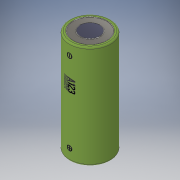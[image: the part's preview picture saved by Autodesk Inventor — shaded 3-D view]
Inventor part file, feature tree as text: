
AUTODESK INVENTOR PART (.ipt)
format: ipt  version: 2019.2 (Build 232265000, 265)  size: 1,053,696 bytes
history: native  units: mm
features: sketch x5, fillet x3, extrude x2, emboss x2, revolve x1, plane x1
ambient origin geometry x8: Origin, YZ Plane, XZ Plane, XY Plane, X Axis, Y Axis, Z Axis, Center Point
bodies: Solid1 (feature_tree)
feature tree (14):
  revolve  "Revolution1"  [1 undecoded]
  fillet  "Fillet1"  [1 undecoded]
  extrude  "Extrusion1"  Depth=13.0mm
  fillet  "Fillet2"  Radius=21.0mm
  sketch  "Sketch5"  dims[d11=2.0mm d12=2.0mm d13=2.0mm d14=2.0mm d15=0.01mm d16=0.174533mm d18=0.1mm d19=8.0mm d20=9.0mm d21=0.01mm d22=0.174533mm d23=3.5mm d24=0.2mm d25=0.0mm d26=0.5mm]
  extrude  "Extrusion2"  Depth=0.5mm
  plane  "Work Plane1"
  emboss  "Emboss1"
  emboss  "Emboss2"
  fillet  "Fillet3"  Radius=2.0mm
  sketch  "Sketch1"  dims[d0=65.0mm d1=13.0mm d2=90.0deg]
  sketch  "Sketch2"  dims[d3=1.0mm d4=13.0mm d5=21.0mm]
  sketch  "Sketch3"  dims[d6=0.2mm d7=0.0mm d8=0.5mm d9=2.0mm]
  sketch  "Sketch4"  dims[d10=2.0mm]
note: 2 required parameter values undecoded (feature->parameter linkage not recoverable at this tier; creation-order binding heuristic only, values carry confidence <= 0.55)